# Revit family: VISS ROUND LED LIGHT
name_source: partatom
category: Lighting Fixtures
units: mm (PartAtom-declared; Revit-internal decimal feet)

## family parameters
Cut with Voids When Loaded = No
Host = Face
Light Source = Yes
Part Type = Normal
Room Calculation Point = No
Round Connector Dimension = Use Diameter
Shared = No

## types (64) — shared parameters
Acoustic = Acoustic -130
Average life based on 77F(HRS) = 50000
B = 0' - 1 3/8"
CRI = 90
Color Filter = 16777215
Default Elevation = 0' - 0"
Description = The Viss Series has an unique square and round style with an LED light source illuminating its inner surface.
Dimming Lamp Color Temperature Shift = <None>
Driver Options = 0-10V
Fixture Height = 0' - 3 1/2"
IP Rating = 20
Load Classification = Lighting
Manufacturer = Above All Lighting
Power Factor = 1
Suspender Height = 4' - 0"
Tilt Angle = 90.00°
Total Length = 5' - 0"
Type Comments = VISS ROUND LED LIGHT Acoustic
URL = https://www.abovealllighting.com
Voltage = 277 V

## per-type parameters (varying)
| type | Acoustic Body | Aircraft Cable Pendant Mount | Apparent Load | B1 | B2 | BODY FINISH | Fixture Diameter | Order number | Photometric Web File | Surface Acoustic Body | Surface Mount | Wattage Comments |
| VSI-R-1514-30901-ACPMK-WH | No | Yes | 19 VA | 0' - 3 9/32" | 0' - 6 25/32" | White | 0' - 7 3/32" | 17592 | VSI-R-1514-30901.IES | No | No | 15W |
| VSI-R-2518-30901-ACPMK-WH | No | Yes | 31 VA | 0' - 5 1/32" | 0' - 8 17/32" | White | 0' - 8 27/32" | 17593 | VSI-R-2518-30901.IES | No | No | 25W |
| VSI-R-3624-30901-ACPMK-WH | No | Yes | 45 VA | 0' - 7 31/32" | 0' - 11 15/32" | White | 0' - 11 13/16" | 17594 | VSI_R_3624_XX901.IES | No | No | 36W |
| VSI-R-5032-30901-ACPMK-WH | No | Yes | 63 VA | 0' - 11 29/32" | 1' - 3 13/32" | White | 1' - 3 3/4" | 17595 | VSI_R_5032_XX901.IES | No | No | 50W |
| VSI-R-1514-40901-ACPMK-WH | No | Yes | 19 VA | 0' - 3 9/32" | 0' - 6 25/32" | White | 0' - 7 3/32" | 17600 | VSI_R_1514_XX901.IES | No | No | 15W |
| VSI-R-2518-40901-ACPMK-WH | No | Yes | 31 VA | 0' - 5 1/32" | 0' - 8 17/32" | White | 0' - 8 27/32" | 17601 | VSI_R_2518_XX901.IES | No | No | 25W |
| VSI-R-3624-40901-ACPMK-WH | No | Yes | 45 VA | 0' - 7 31/32" | 0' - 11 15/32" | White | 0' - 11 13/16" | 17602 | VSI-S-3624-40901.IES | No | No | 36W |
| VSI-R-5032-40901-ACPMK-WH | No | Yes | 63 VA | 0' - 11 29/32" | 1' - 3 13/32" | White | 1' - 3 3/4" | 17603 | VSI-R-5032-40901.IES | No | No | 50W |
| VSI-R-LA-1514-30901-ACPMK-WH-NSAC-021 130 | Yes | Yes | 19 VA | 0' - 3 9/32" | 0' - 6 25/32" | White | 0' - 7 3/32" | 17608 | VSI_R_1514_with_acoustic.IES | No | No | 15W |
| VSI-R-LA-2518-30901-ACPMK-WH-NSAC-021 130 | Yes | Yes | 31 VA | 0' - 5 1/32" | 0' - 8 17/32" | White | 0' - 8 27/32" | 17609 | VSI_R_2518_with_acoustic.IES | No | No | 25W |
| VSI-R-LA-3624-30901-ACPMK-WH-NSAC-021 130 | Yes | Yes | 45 VA | 0' - 7 31/32" | 0' - 11 15/32" | White | 0' - 11 13/16" | 17610 | VSI_R_3624_with_acoustic.IES | No | No | 36W |
| VSI-R-LA-5032-30901-ACPMK-WH-NSAC-021 130 | Yes | Yes | 63 VA | 0' - 11 29/32" | 1' - 3 13/32" | White | 1' - 3 3/4" | 17611 | VSI_R_5032_with_acoustic.IES | No | No | 50W |
| VSI-R-LA-1514-40901-ACPMK-WH-NSAC-021 130 | Yes | Yes | 19 VA | 0' - 3 9/32" | 0' - 6 25/32" | White | 0' - 7 3/32" | 17616 | VSI_R_1514_with_acoustic.IES | No | No | 15W |
| VSI-R-LA-2518-40901-ACPMK-WH-NSAC-021 130 | Yes | Yes | 31 VA | 0' - 5 1/32" | 0' - 8 17/32" | White | 0' - 8 27/32" | 17617 | VSI_R_2518_with_acoustic.IES | No | No | 25W |
| VSI-R-LA-3624-40901-ACPMK-WH-NSAC-021 130 | Yes | Yes | 45 VA | 0' - 7 31/32" | 0' - 11 15/32" | White | 0' - 11 13/16" | 17618 | VSI_R_3624_with_acoustic.IES | No | No | 36W |
| VSI-R-LA-5032-40901-ACPMK-WH-NSAC-021 130 | Yes | Yes | 63 VA | 0' - 11 29/32" | 1' - 3 13/32" | White | 1' - 3 3/4" | 17619 | VSI_R_5032_with_acoustic.IES | No | No | 50W |
| VSI-R-1514-30901-SMK-WH | No | No | 19 VA | 0' - 3 9/32" | 0' - 6 25/32" | White | 0' - 7 3/32" | 17657 | VSI-R-1514-30901.IES | No | Yes | 15W |
| VSI-R-LA-1514-30901-SMK-WH-NSAC-021 130 | No | No | 19 VA | 0' - 3 9/32" | 0' - 6 25/32" | White | 0' - 7 3/32" | 17673 | VSI_R_1514_with_acoustic.IES | Yes | Yes | 15W |
| VSI-R-2518-30901-SMK-WH | No | No | 31 VA | 0' - 5 1/32" | 0' - 8 17/32" | White | 0' - 8 27/32" | 17658 | VSI-R-2518-30901.IES | No | Yes | 25W |
| VSI-R-3624-30901-SMK-WH | No | No | 45 VA | 0' - 7 31/32" | 0' - 11 15/32" | White | 0' - 11 13/16" | 17659 | VSI_R_3624_XX901.IES | No | Yes | 36W |
| VSI-R-5032-30901-SMK-WH | No | No | 63 VA | 0' - 11 29/32" | 1' - 3 13/32" | White | 1' - 3 3/4" | 17660 | VSI_R_5032_XX901.IES | No | Yes | 50W |
| VSI-R-1514-40901-SMK-WH | No | No | 19 VA | 0' - 3 9/32" | 0' - 6 25/32" | White | 0' - 7 3/32" | 17665 | VSI_R_1514_XX901.IES | No | Yes | 15W |
| VSI-R-2518-40901-SMK-WH | No | No | 31 VA | 0' - 5 1/32" | 0' - 8 17/32" | White | 0' - 8 27/32" | 17666 | VSI_R_2518_XX901.IES | No | Yes | 25W |
| VSI-R-3624-40901-SMK-WH | No | No | 45 VA | 0' - 7 31/32" | 0' - 11 15/32" | White | 0' - 11 13/16" | 17667 | VSI-R-3624-40901.IES | No | Yes | 36W |
| VSI-R-5032-40901-SMK-WH | No | No | 63 VA | 0' - 11 29/32" | 1' - 3 13/32" | White | 1' - 3 3/4" | 17668 | VSI-R-5032-40901.IES | No | Yes | 50W |
| VSI-R-LA-2518-30901-SMK-WH-NSAC-021 130 | No | No | 31 VA | 0' - 5 1/32" | 0' - 8 17/32" | White | 0' - 8 27/32" | 17674 | VSI_R_2518_with_acoustic.IES | Yes | Yes | 25W |
| VSI-R-LA-3624-30901-SMK-WH-NSAC-021 130 | No | No | 45 VA | 0' - 7 31/32" | 0' - 11 15/32" | White | 0' - 11 13/16" | 17675 | VSI_R_3624_with_acoustic.IES | Yes | Yes | 36W |
| VSI-R-LA-5032-30901-SMK-WH-NSAC-021 130 | No | No | 63 VA | 0' - 11 29/32" | 1' - 3 13/32" | White | 1' - 3 3/4" | 17676 | VSI_R_5032_with_acoustic.IES | Yes | Yes | 50W |
| VSI-R-LA-1514-40901-SMK-WH-NSAC-021 130 | No | No | 19 VA | 0' - 3 9/32" | 0' - 6 25/32" | White | 0' - 7 3/32" | 17681 | VSI_R_1514_with_acoustic.IES | Yes | Yes | 15W |
| VSI-R-LA-2518-40901-SMK-WH-NSAC-021 130 | No | No | 31 VA | 0' - 5 1/32" | 0' - 8 17/32" | White | 0' - 8 27/32" | 17682 | VSI_R_2518_with_acoustic.IES | Yes | Yes | 25W |
| VSI-R-LA-3624-40901-SMK-WH-NSAC-021 130 | No | No | 45 VA | 0' - 7 31/32" | 0' - 11 15/32" | White | 0' - 11 13/16" | 17683 | VSI_R_3624_with_acoustic.IES | Yes | Yes | 36W |
| VSI-R-LA-5032-40901-SMK-WH-NSAC-021 130 | No | No | 63 VA | 0' - 11 29/32" | 1' - 3 13/32" | White | 1' - 3 3/4" | 17684 | VSI_R_5032_with_acoustic.IES | Yes | Yes | 50W |
| VSI-R-1514-30901-ACPMK-BK | No | Yes | 19 VA | 0' - 3 9/32" | 0' - 6 25/32" | Black | 0' - 7 3/32" | 17596 | VSI-R-1514-30901.IES | No | No | 15W |
| VSI-R-2518-30901-ACPMK-BK | No | Yes | 31 VA | 0' - 5 1/32" | 0' - 8 17/32" | Black | 0' - 8 27/32" | 17597 | VSI-R-2518-30901.IES | No | No | 25W |
| VSI-R-3624-30901-ACPMK-BK | No | Yes | 45 VA | 0' - 7 31/32" | 0' - 11 15/32" | Black | 0' - 11 13/16" | 17598 | VSI_R_3624_XX901.IES | No | No | 36W |
| VSI-R-5032-30901-ACPMK-BK | No | Yes | 63 VA | 0' - 11 29/32" | 1' - 3 13/32" | Black | 1' - 3 3/4" | 17599 | VSI_R_5032_XX901.IES | No | No | 50W |
| VSI-R-1514-40901-ACPMK-BK | No | Yes | 19 VA | 0' - 3 9/32" | 0' - 6 25/32" | Black | 0' - 7 3/32" | 17604 | VSI_R_1514_XX901.IES | No | No | 15W |
| VSI-R-2518-40901-ACPMK-BK | No | Yes | 31 VA | 0' - 5 1/32" | 0' - 8 17/32" | Black | 0' - 8 27/32" | 17605 | VSI_R_2518_XX901.IES | No | No | 25W |
| VSI-R-3624-40901-ACPMK-BK | No | Yes | 45 VA | 0' - 7 31/32" | 0' - 11 15/32" | Black | 0' - 11 13/16" | 17606 | VSI-R-3624-40901.IES | No | No | 36W |
| VSI-R-5032-40901-ACPMK-BK | No | Yes | 63 VA | 0' - 11 29/32" | 1' - 3 13/32" | Black | 1' - 3 3/4" | 17607 | VSI-R-5032-40901.IES | No | No | 50W |
| VSI-R-1514-30901-SMK-BK | No | No | 19 VA | 0' - 3 9/32" | 0' - 6 25/32" | Black | 0' - 7 3/32" | 17661 | VSI-R-1514-30901.IES | No | Yes | 15W |
| VSI-R-2518-30901-SMK-BK | No | No | 31 VA | 0' - 5 1/32" | 0' - 8 17/32" | Black | 0' - 8 27/32" | 17662 | VSI-R-2518-30901.IES | No | Yes | 25W |
| VSI-R-3624-30901-SMK-BK | No | No | 45 VA | 0' - 7 31/32" | 0' - 11 15/32" | Black | 0' - 11 13/16" | 17663 | VSI_R_3624_XX901.IES | No | Yes | 36W |
| VSI-R-5032-30901-SMK-BK | No | No | 63 VA | 0' - 11 29/32" | 1' - 3 13/32" | Black | 1' - 3 3/4" | 17664 | VSI_R_5032_XX901.IES | No | Yes | 50W |
| VSI-R-1514-40901-SMK-BK | No | No | 19 VA | 0' - 3 9/32" | 0' - 6 25/32" | Black | 0' - 7 3/32" | 17669 | VSI_R_1514_XX901.IES | No | Yes | 15W |
| VSI-R-2518-40901-SMK-BK | No | No | 31 VA | 0' - 5 1/32" | 0' - 8 17/32" | Black | 0' - 8 27/32" | 17670 | VSI_R_2518_XX901.IES | No | Yes | 25W |
| VSI-R-3624-40901-SMK-BK | No | No | 45 VA | 0' - 7 31/32" | 0' - 11 15/32" | Black | 0' - 11 13/16" | 17671 | VSI-R-3624-40901.IES | No | Yes | 36W |
| VSI-R-5032-40901-SMK-BK | No | No | 63 VA | 0' - 11 29/32" | 1' - 3 13/32" | Black | 1' - 3 3/4" | 17672 | VSI-R-5032-40901.IES | No | Yes | 50W |
| VSI-R-LA-1514-30901-ACPMK-BK-NSAC-021 130 | Yes | Yes | 19 VA | 0' - 3 9/32" | 0' - 6 25/32" | Black | 0' - 7 3/32" | 17612 | VSI_R_1514_with_acoustic.IES | No | No | 15W |
| VSI-R-LA-2518-30901-ACPMK-BK-NSAC-021 130 | Yes | Yes | 31 VA | 0' - 5 1/32" | 0' - 8 17/32" | Black | 0' - 8 27/32" | 17613 | VSI_R_2518_with_acoustic.IES | No | No | 25W |
| VSI-R-LA-3624-30901-ACPMK-BK-NSAC-021 130 | Yes | Yes | 45 VA | 0' - 7 31/32" | 0' - 11 15/32" | Black | 0' - 11 13/16" | 17614 | VSI_R_3624_with_acoustic.IES | No | No | 36W |
| VSI-R-LA-5032-30901-ACPMK-BK-NSAC-021 130 | Yes | Yes | 63 VA | 0' - 11 29/32" | 1' - 3 13/32" | Black | 1' - 3 3/4" | 17615 | VSI_R_5032_with_acoustic.IES | No | No | 50W |
| VSI-R-LA-1514-40901-ACPMK-BK-NSAC-021 130 | Yes | Yes | 19 VA | 0' - 3 9/32" | 0' - 6 25/32" | Black | 0' - 7 3/32" | 17620 | VSI_R_1514_with_acoustic.IES | No | No | 15W |
| VSI-R-LA-2518-40901-ACPMK-BK-NSAC-021 130 | Yes | Yes | 31 VA | 0' - 5 1/32" | 0' - 8 17/32" | Black | 0' - 8 27/32" | 17621 | VSI_R_2518_with_acoustic.IES | No | No | 25W |
| VSI-R-LA-3624-40901-ACPMK-BK-NSAC-021 130 | Yes | Yes | 45 VA | 0' - 7 31/32" | 0' - 11 15/32" | Black | 0' - 11 13/16" | 17622 | VSI_R_3624_with_acoustic.IES | No | No | 36W |
| VSI-R-LA-5032-40901-ACPMK-BK-NSAC-021 130 | Yes | Yes | 63 VA | 0' - 11 29/32" | 1' - 3 13/32" | Black | 1' - 3 3/4" | 17623 | VSI_R_5032_with_acoustic.IES | No | No | 50W |
| VSI-R-LA-1514-30901-SMK-BK-NSAC-021 130 | No | No | 19 VA | 0' - 3 9/32" | 0' - 6 25/32" | Black | 0' - 7 3/32" | 17677 | VSI_R_1514_with_acoustic.IES | Yes | Yes | 15W |
| VSI-R-LA-2518-30901-SMK-BK-NSAC-021 130 | No | No | 31 VA | 0' - 5 1/32" | 0' - 8 17/32" | Black | 0' - 8 27/32" | 17678 | VSI_R_2518_with_acoustic.IES | Yes | Yes | 25W |
| VSI-R-LA-3624-30901-SMK-BK-NSAC-021 130 | No | No | 45 VA | 0' - 7 31/32" | 0' - 11 15/32" | Black | 0' - 11 13/16" | 17679 | VSI_R_3624_with_acoustic.IES | Yes | Yes | 36W |
| VSI-R-LA-5032-30901-SMK-BK-NSAC-021 130 | No | No | 63 VA | 0' - 11 29/32" | 1' - 3 13/32" | Black | 1' - 3 3/4" | 17680 | VSI_R_5032_with_acoustic.IES | Yes | Yes | 50W |
| VSI-R-LA-1514-40901-SMK-BK-NSAC-021 130 | No | No | 19 VA | 0' - 3 9/32" | 0' - 6 25/32" | Black | 0' - 7 3/32" | 17685 | VSI_R_1514_with_acoustic.IES | Yes | Yes | 15W |
| VSI-R-LA-2518-40901-SMK-BK-NSAC-021 130 | No | No | 31 VA | 0' - 5 1/32" | 0' - 8 17/32" | Black | 0' - 8 27/32" | 17686 | VSI_R_2518_with_acoustic.IES | Yes | Yes | 25W |
| VSI-R-LA-3624-40901-SMK-BK-NSAC-021 130 | No | No | 45 VA | 0' - 7 31/32" | 0' - 11 15/32" | Black | 0' - 11 13/16" | 17687 | VSI_R_3624_with_acoustic.IES | Yes | Yes | 36W |
| VSI-R-LA-5032-40901-SMK-BK-NSAC-021 130 | No | No | 63 VA | 0' - 11 29/32" | 1' - 3 13/32" | Black | 1' - 3 3/4" | 17688 | VSI_R_5032_with_acoustic.IES | Yes | Yes | 50W |

note: column(s) folded — value = type name in every type: Model

## geometry (parser evidence)
native form markers: Sweep x11
no freeform markers — native parametric forms only
